# Revit family: POR_Ulysse_P1254_BIM_FR
name_source: partatom
category: Plumbing Fixtures
revit_build: Autodesk Revit MEP 2014 (Build: 20130308_1515(x64)
units: mm (PartAtom-declared; Revit-internal decimal feet)

## types (1)
- P1254 - ULYSSE LAVABO 50X44 BLANC
    Accessoires = www.idealspec.fr
    Assembly Code = C1030200
    Auteur = www.idealstandardinternational.com
    Bim-NomDuProjet = POR_Porcher_WashbasinSystems_Ulysse_P125401
    CWFU = 0
    Caractéristiques = Lavabo-plan mural- P125401/ Porcher
    Conformité = NF
    ConseilsDInstallation = www.idealspec.fr
    Cost = 0 $
    Couleur = Blanc
    CoûtDeRemplacement = 0
    DateDeCréation = 2016-11-11
    Default Elevation = 861 mm
    Description = Ulysse Lavabo 50x44 Blanc
    DiamètreÉvacuation = 0
    Dimensions = 445 x 507 x 861 mm
    DuréeDeGarantieDesPièces = 2
    DuréeGarantie = ans
    DébitL/Mn = 0
    DétailGarantie = Constructeur
    Espace = Interne
    Finition = Blanc
    Forme = Complexe
    HWFU = 0
    Hauteur = 861 mm
    IfcExportAs = IfcSanitaryType
    IfcExportType = WASHHANDBASINS
    InformationsProduit = www.idealspec.fr
    Largeur = 506 mm
    Longueur = 444 mm
    Marque = PORCHER
    Matériel = Céramique
    Model = P125401
    Montage/PoseDuLavabo = Murale
    Nom = WashbasinSystems_Ulysse_P125401_Porcher
    PerformanceAccessibilité = NF
    PoidsNet = 14 kg
    Profondeur = 444 mm
    Raccordement = Plomberie
    Révision = 1
    TypeDImmobilisation = Fixe
    URL = www.idealspec.fr
    Uniclass2015Code = Ss_40_15_75_94
    Uniclass2015Title = Washbasin systems
    Uniclass2015Version = Products v1.1
    UnitéDeTemps = an
    UrlDuFabricant = www.idealspec.fr
    Version = 1
    WFU = 0

## geometry (parser evidence)
native form markers: Sweep x4
no freeform markers — native parametric forms only
